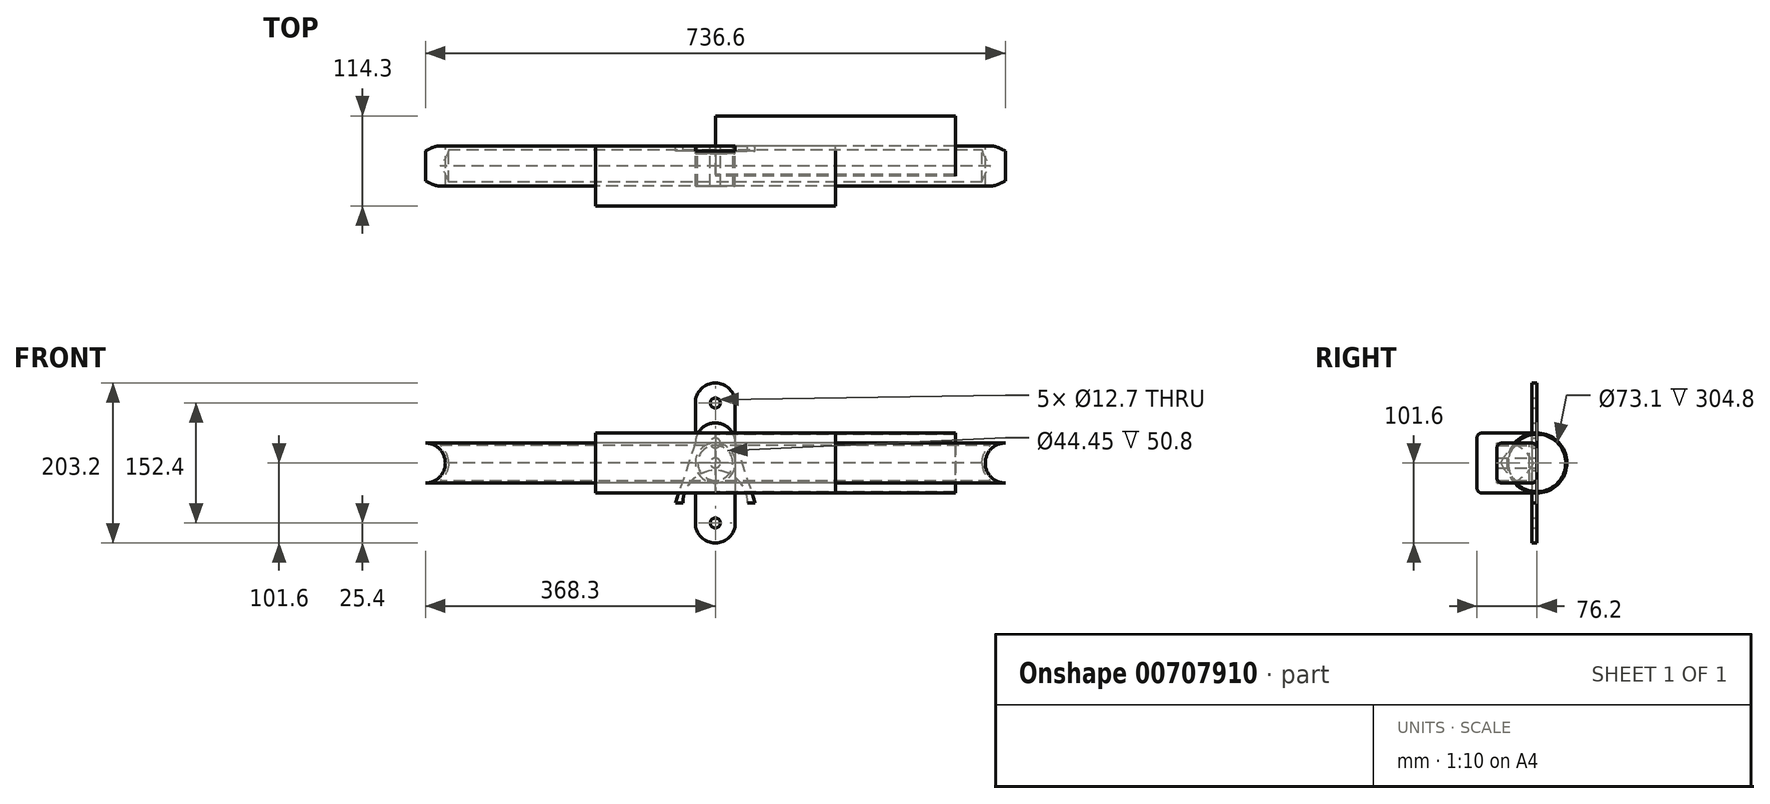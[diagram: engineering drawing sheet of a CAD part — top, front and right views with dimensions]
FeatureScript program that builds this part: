
annotation { "Feature Type Name" : "Feature", "Feature Type Description" : "" }
export const myFeature = defineFeature(function(context is Context, id is Id, definition is map)
    precondition{}
    {
        {
            var Q0;
            Q0=qCreatedBy(makeId("Front.planeOp"),FACE);
            var sketch = newSketch(context, id + "F0", { "sketchPlane" : qUnion([Q0])});
            skLineSegment(sketch, "E0.bottom", {"start": v(368.3, 25.4) * mm, "end": v(-368.3, 25.4) * mm});
            skLineSegment(sketch, "E0.top", {"start": v(368.3, -25.4) * mm, "end": v(-368.3, -25.4) * mm});
            skPoint(sketch, "E0.middle", {"position": v(0, 0) * mm});
            skArc(sketch, "E1", {"start": v(-368.3, -25.4) * mm, "mid": v(-342.9, 0) * mm, "end": v(-368.3, 25.4) * mm});
            skArc(sketch, "E2", {"start": v(368.3, 25.4) * mm, "mid": v(342.9, 0) * mm, "end": v(368.3, -25.4) * mm});
            skSolve(sketch);
        }
        {
            var Q0;
            Q0 = qSketchRegion(id + "F0", true);
            extrude(context, id + "F1", {"entities" : qUnion([Q0]), "depth" : 50.8 * mm, "offsetDistance" : 25.4 * mm});
        }
        {
            var Q0;
            Q0=makeQuery(id+"F1.opExtrude","CAP_EDGE",EDGE,{"disambiguationData":[OSD([sQuery(id+"F0.wireOp",EDGE,"E0.top")])],"isStart":false});
            var Q1;
            Q1=makeQuery(id+"F1.opExtrude","CAP_EDGE",EDGE,{"disambiguationData":[OSD([sQuery(id+"F0.wireOp",EDGE,"E0.bottom")])],"isStart":false});
            var Q2;
            Q2=makeQuery(id+"F1.opExtrude","CAP_EDGE",EDGE,{"disambiguationData":[OSD([sQuery(id+"F0.wireOp",EDGE,"E0.bottom")])],"isStart":true});
            var Q3;
            Q3=makeQuery(id+"F1.opExtrude","CAP_EDGE",EDGE,{"disambiguationData":[OSD([sQuery(id+"F0.wireOp",EDGE,"E0.top")])],"isStart":true});
            fillet(context, id + "F2", {"entities" : qUnion([Q0, Q1, Q2, Q3]), "radius" : 6.35 * mm, "tangentPropagation" : true, "allowEdgeOverflow" : false});
        }
        {
            var Q0;
            Q0=qCreatedBy(makeId("Front.planeOp"),FACE);
            var sketch = newSketch(context, id + "F3", { "sketchPlane" : qUnion([Q0])});
            skCircle(sketch, "E3", {"center": v(0, 0) * mm, "radius": 25.4 * mm});
            skCircle(sketch, "E4", {"center": v(0, 0) * mm, "radius": 22.23 * mm});
            skSolve(sketch);
        }
        {
            var Q0;
            Q0 = qSketchRegion(id + "F3", true);
            extrude(context, id + "F4", {"entities" : qUnion([Q0]), "depth" : 50.8 * mm, "offsetDistance" : 25.4 * mm});
        }
        {
            var Q0;
            Q0=qCreatedBy(makeId("Front.planeOp"),FACE);
            var sketch = newSketch(context, id + "F5", { "sketchPlane" : qUnion([Q0])});
            skLineSegment(sketch, "E5.bottom", {"start": v(368.3, 29.46) * mm, "end": v(-368.3, 29.46) * mm});
            skLineSegment(sketch, "E5.top", {"start": v(368.3, -29.46) * mm, "end": v(-368.3, -29.46) * mm});
            skPoint(sketch, "E5.middle", {"position": v(0, 0) * mm});
            skArc(sketch, "E6", {"start": v(368.3, 29.46) * mm, "mid": v(338.84, 0) * mm, "end": v(368.3, -29.46) * mm});
            skArc(sketch, "E7", {"start": v(-368.3, -29.46) * mm, "mid": v(-338.84, 0) * mm, "end": v(-368.3, 29.46) * mm});
            skSolve(sketch);
        }
        {
            var Q0;
            Q0 = qSketchRegion(id + "F5", true);
            extrude(context, id + "F6", {"entities" : qUnion([Q0]), "depth" : 50.8 * mm, "offsetDistance" : 25.4 * mm});
        }
        {
            var Q0;
            Q0=makeQuery(id+"F6.opExtrude","CAP_EDGE",EDGE,{"disambiguationData":[OSD([sQuery(id+"F5.wireOp",EDGE,"E5.top")])],"isStart":false});
            var Q1;
            Q1=makeQuery(id+"F6.opExtrude","CAP_EDGE",EDGE,{"disambiguationData":[OSD([sQuery(id+"F5.wireOp",EDGE,"E5.bottom")])],"isStart":false});
            var Q2;
            Q2=makeQuery(id+"F6.opExtrude","CAP_EDGE",EDGE,{"disambiguationData":[OSD([sQuery(id+"F5.wireOp",EDGE,"E5.top")])],"isStart":true});
            var Q3;
            Q3=makeQuery(id+"F6.opExtrude","CAP_EDGE",EDGE,{"disambiguationData":[OSD([sQuery(id+"F5.wireOp",EDGE,"E5.bottom")])],"isStart":true});
            fillet(context, id + "F7", {"entities" : qUnion([Q0, Q1, Q2, Q3]), "radius" : 50.8 * mm, "tangentPropagation" : true, "allowEdgeOverflow" : false});
        }
        {
            var Q0;
            Q0=qCreatedBy(makeId("Front.planeOp"),FACE);
            var sketch = newSketch(context, id + "F8", { "sketchPlane" : qUnion([Q0])});
            skLineSegment(sketch, "E8.top", {"start": v(50.8, -50.8) * mm, "end": v(41.27, -50.8) * mm});
            skPoint(sketch, "E8.middle", {"position": v(0, 0) * mm});
            skArc(sketch, "E9", {"start": v(25.4, 25.4) * mm, "mid": v(0, 50.8) * mm, "end": v(-25.4, 25.4) * mm});
            skPoint(sketch, "E10.start.orphan", {"position": v(0, 50.8) * mm});
            skLineSegment(sketch, "E11", {"start": v(25.4, 25.4) * mm, "end": v(50.8, -50.8) * mm});
            skLineSegment(sketch, "E12", {"start": v(-25.4, 25.4) * mm, "end": v(-50.8, -50.8) * mm});
            skPoint(sketch, "E8.left.start.orphan", {"position": v(50.8, 50.8) * mm});
            skPoint(sketch, "E8.right.start.orphan", {"position": v(-50.8, 50.8) * mm});
            skCircle(sketch, "E13", {"center": v(0, 25.4) * mm, "radius": 6.35 * mm});
            skArc(sketch, "E14", {"start": v(41.27, -50.8) * mm, "mid": v(0, -9.53) * mm, "end": v(-41.28, -50.8) * mm});
            skLineSegment(sketch, "E15.trimOffspring", {"start": v(-41.28, -50.8) * mm, "end": v(-50.8, -50.8) * mm});
            skSolve(sketch);
        }
        {
            var Q0;
            Q0 = qSketchRegion(id + "F8", true);
            extrude(context, id + "F9", {"entities" : qUnion([Q0]), "depth" : 6.35 * mm, "offsetDistance" : 25.4 * mm});
        }
        {
            var Q0;
            Q0=qCreatedBy(makeId("Front.planeOp"),FACE);
            var sketch = newSketch(context, id + "F10", { "sketchPlane" : qUnion([Q0])});
            skCircle(sketch, "E16", {"center": v(0, 0) * mm, "radius": 22.23 * mm});
            skCircle(sketch, "E17", {"center": v(0, 0) * mm, "radius": 6.35 * mm});
            skSolve(sketch);
        }
        {
            var Q0;
            Q0 = qSketchRegion(id + "F10", true);
            extrude(context, id + "F11", {"entities" : qUnion([Q0]), "depth" : 50.8 * mm, "offsetDistance" : 25.4 * mm});
        }
        {
            var Q0;
            Q0=qCreatedBy(makeId("Front.planeOp"),FACE);
            var sketch = newSketch(context, id + "F12", { "sketchPlane" : qUnion([Q0])});
            skCircle(sketch, "E18", {"center": v(0, 0) * mm, "radius": 25.4 * mm});
            skCircle(sketch, "E19", {"center": v(0, 0) * mm, "radius": 6.35 * mm});
            skSolve(sketch);
        }
        {
            var Q0;
            Q0 = qSketchRegion(id + "F12", true);
            extrude(context, id + "F13", {"entities" : qUnion([Q0]), "depth" : 9.52 * mm, "offsetDistance" : 25.4 * mm});
        }
        {
            var Q0;
            Q0=qCreatedBy(makeId("Right.planeOp"),FACE);
            var sketch = newSketch(context, id + "F14", { "sketchPlane" : qUnion([Q0])});
            skCircle(sketch, "E20", {"center": v(0, 0) * mm, "radius": 38.1 * mm});
            skCircle(sketch, "E21", {"center": v(0, 0) * mm, "radius": 36.55 * mm});
            skSolve(sketch);
        }
        {
            var Q0;
            Q0 = qSketchRegion(id + "F14", true);
            extrude(context, id + "F15", {"entities" : qUnion([Q0]), "depth" : 304.8 * mm, "offsetDistance" : 25.4 * mm});
        }
        {
            var Q0;
            Q0=qCreatedBy(makeId("Front.planeOp"),FACE);
            var sketch = newSketch(context, id + "F16", { "sketchPlane" : qUnion([Q0])});
            skLineSegment(sketch, "E22.left", {"start": v(25.4, 76.2) * mm, "end": v(25.4, -76.2) * mm});
            skLineSegment(sketch, "E22.right", {"start": v(-25.4, 76.2) * mm, "end": v(-25.4, 38.1) * mm});
            skPoint(sketch, "E22.middle", {"position": v(0, 0) * mm});
            skPoint(sketch, "E23.endSnap0", {"position": v(0, 101.6) * mm});
            skArc(sketch, "E24", {"start": v(25.4, 76.2) * mm, "mid": v(0, 101.6) * mm, "end": v(-25.4, 76.2) * mm});
            skPoint(sketch, "E25.orphan", {"position": v(25.4, 101.6) * mm});
            skPoint(sketch, "E22.bottom.end.orphan", {"position": v(-25.4, 101.6) * mm});
            skPoint(sketch, "E23.start.orphan", {"position": v(0, 101.6) * mm});
            skArc(sketch, "E26", {"start": v(-25.4, -76.2) * mm, "mid": v(0, -101.6) * mm, "end": v(25.4, -76.2) * mm});
            skPoint(sketch, "E27.orphan", {"position": v(25.4, -101.6) * mm});
            skPoint(sketch, "E28.orphan", {"position": v(-25.4, -101.6) * mm});
            skCircle(sketch, "E29", {"center": v(0, 76.2) * mm, "radius": 6.35 * mm});
            skPoint(sketch, "E30.start.orphan", {"position": v(0, -101.6) * mm});
            skCircle(sketch, "E31", {"center": v(0, -76.2) * mm, "radius": 6.35 * mm});
            skLineSegment(sketch, "E32.bottom", {"start": v(0, 38.1) * mm, "end": v(-25.4, 38.1) * mm});
            skLineSegment(sketch, "E32.top", {"start": v(0, -38.1) * mm, "end": v(-25.4, -38.1) * mm});
            skLineSegment(sketch, "E32.left", {"start": v(0, 38.1) * mm, "end": v(0, -38.1) * mm});
            skPoint(sketch, "E32.middle", {"position": v(-25.4, 0) * mm});
            skPoint(sketch, "E32.right.start.orphan", {"position": v(-50.8, 38.1) * mm});
            skPoint(sketch, "E33.orphan", {"position": v(-50.8, -38.1) * mm});
            skLineSegment(sketch, "E34.trimOffspring", {"start": v(-25.4, -38.1) * mm, "end": v(-25.4, -76.2) * mm});
            skSolve(sketch);
        }
        {
            var Q0;
            Q0 = qSketchRegion(id + "F16", true);
            extrude(context, id + "F17", {"entities" : qUnion([Q0]), "depth" : 6.35 * mm, "offsetDistance" : 25.4 * mm});
        }
        {
            var Q0;
            Q0=qCreatedBy(makeId("Front.planeOp"),FACE);
            var sketch = newSketch(context, id + "F18", { "sketchPlane" : qUnion([Q0])});
            skLineSegment(sketch, "E35.bottom", {"start": v(152.4, 38.1) * mm, "end": v(-152.4, 38.1) * mm});
            skLineSegment(sketch, "E35.top", {"start": v(152.4, -38.1) * mm, "end": v(-152.4, -38.1) * mm});
            skLineSegment(sketch, "E35.left", {"start": v(152.4, 38.1) * mm, "end": v(152.4, -38.1) * mm});
            skLineSegment(sketch, "E35.right", {"start": v(-152.4, 38.1) * mm, "end": v(-152.4, -38.1) * mm});
            skPoint(sketch, "E35.middle", {"position": v(0, 0) * mm});
            skSolve(sketch);
        }
        {
            var Q0;
            Q0 = qSketchRegion(id + "F18", true);
            extrude(context, id + "F19", {"entities" : qUnion([Q0]), "depth" : 76.2 * mm, "offsetDistance" : 25.4 * mm});
        }
        {
            var Q0;
            Q0=makeQuery(id+"F19.opExtrude","CAP_EDGE",EDGE,{"disambiguationData":[OSD([sQuery(id+"F18.wireOp",EDGE,"E35.bottom")])],"isStart":false});
            var Q1;
            Q1=makeQuery(id+"F19.opExtrude","CAP_EDGE",EDGE,{"disambiguationData":[OSD([sQuery(id+"F18.wireOp",EDGE,"E35.top")])],"isStart":false});
            var Q2;
            Q2=makeQuery(id+"F19.opExtrude","CAP_EDGE",EDGE,{"disambiguationData":[OSD([sQuery(id+"F18.wireOp",EDGE,"E35.bottom")])],"isStart":true});
            var Q3;
            Q3=makeQuery(id+"F19.opExtrude","CAP_EDGE",EDGE,{"disambiguationData":[OSD([sQuery(id+"F18.wireOp",EDGE,"E35.top")])],"isStart":true});
            fillet(context, id + "F20", {"entities" : qUnion([Q0, Q1, Q2, Q3]), "radius" : 6.35 * mm, "tangentPropagation" : true, "allowEdgeOverflow" : false});
        }
    });
